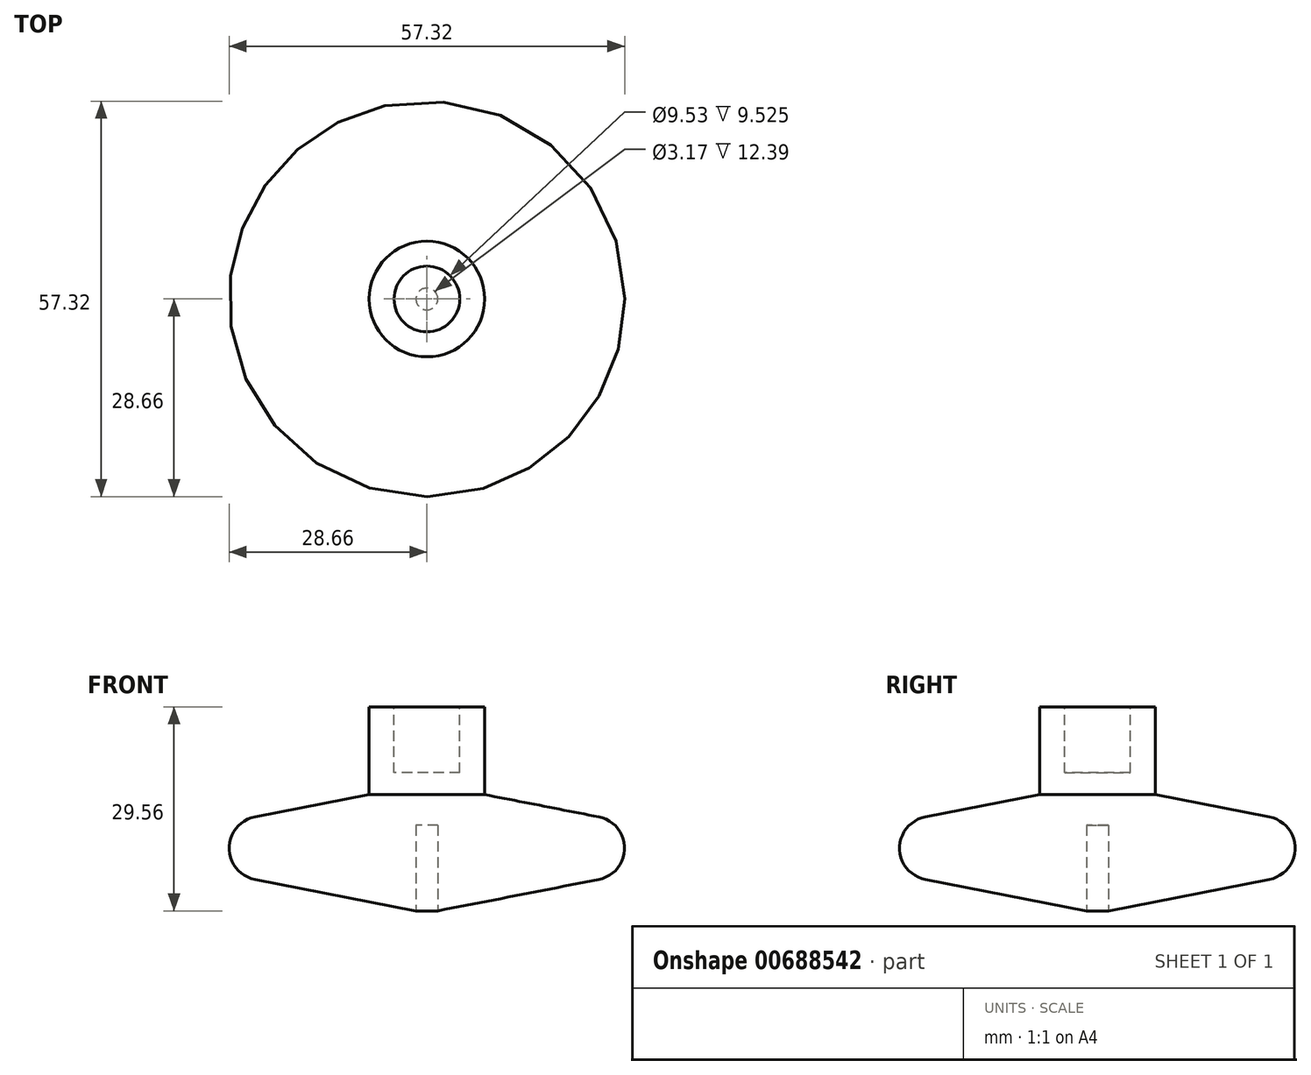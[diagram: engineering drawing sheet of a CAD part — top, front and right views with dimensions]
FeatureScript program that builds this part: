
annotation { "Feature Type Name" : "Feature", "Feature Type Description" : "" }
export const myFeature = defineFeature(function(context is Context, id is Id, definition is map)
    precondition{}
    {
        {
            var Q0;
            Q0=qCreatedBy(makeId("Front.planeOp"),FACE);
            var sketch = newSketch(context, id + "F0", { "sketchPlane" : qUnion([Q0])});
            skLineSegment(sketch, "E0", {"start": v(0, 0) * mm, "end": v(24.93, 4.87) * mm});
            skArc(sketch, "E1", {"start": v(24.93, 4.87) * mm, "mid": v(28.66, 9.4) * mm, "end": v(24.93, 13.93) * mm});
            skLineSegment(sketch, "E2", {"start": v(24.93, 13.93) * mm, "end": v(8.38, 17.17) * mm});
            skLineSegment(sketch, "E3", {"start": v(8.38, 17.17) * mm, "end": v(8.38, 29.87) * mm});
            skLineSegment(sketch, "E4", {"start": v(8.38, 29.87) * mm, "end": v(0, 29.87) * mm});
            skLineSegment(sketch, "E5", {"start": v(0, 29.87) * mm, "end": v(0, 0) * mm});
            skSolve(sketch);
        }
        {
            var Q0;
            Q0 = qSketchRegion(id + "F0", true);
            var Q1;
            Q1 = qConstructionFilter(qBodyType(qCreatedBy(id + "F0" ,EDGE), BodyType.WIRE), ConstructionObject.NO);
            var Q2;
            Q2=sQuery(id+"F0.wireOp",EDGE,"E5");
            revolve(context, id + "F1", {"entities" : qUnion([Q0]), "surfaceEntities" : qUnion([Q1]), "axis" : qUnion([Q2]), "revolveType" : RevolveType.FULL});
        }
        {
            var Q0;
            Q0=makeQuery(id+"F1.opRevolve","SWEPT_FACE",FACE,{"disambiguationData":[OSD([sQuery(id+"F0.wireOp",EDGE,"E4")])]});
            var sketch = newSketch(context, id + "F2", { "sketchPlane" : qUnion([Q0])});
            skCircle(sketch, "E6", {"center": v(0, 0) * mm, "radius": 4.76 * mm});
            skSolve(sketch);
        }
        {
            var Q0;
            Q0 = qSketchRegion(id + "F2", true);
            extrude(context, id + "F3", {"entities" : qUnion([Q0]), "operationType" : NewBodyOperationType.REMOVE, "oppositeDirection" : true, "depth" : 9.52 * mm, "offsetDistance" : 25.4 * mm});
        }
        {
            var Q0;
            Q0=qCreatedBy(makeId("Top.planeOp"),FACE);
            var sketch = newSketch(context, id + "F4", { "sketchPlane" : qUnion([Q0])});
            skCircle(sketch, "E7", {"center": v(0, 0) * mm, "radius": 1.59 * mm});
            skSolve(sketch);
        }
        {
            var Q0;
            Q0 = qSketchRegion(id + "F4", true);
            extrude(context, id + "F5", {"entities" : qUnion([Q0]), "operationType" : NewBodyOperationType.REMOVE, "depth" : 12.7 * mm, "offsetDistance" : 25.4 * mm});
        }
    });
